# Revit family: agtatec_Record_SldngDrset_E-STA_WallBased
name_source: partatom
category: Doors
revit_build: Autodesk Revit Architecture 2015 (Build: 20140606_1530(x64)
units: mm (PartAtom-declared; Revit-internal decimal feet)

## types (12) — shared parameters
AccessoryOptions = Contact manufacturer
AcousticRating = None
AlternativeDoorsetGlazing = Part of glazing spec
AntiFingerTrapRequirement = Yes
Assembly Code = B2030110
BIMObjectName = agtatec_Record_SlidingDoorset_E-STA_WallBased
ClearHeightOfPassage = 2187.00 mm
ClearanceZones = No
Colour = Customer specific
Configuration = 1 or 2
Construction Type = Automatic Sliding Door
Description = Automatic Sliding Door
DoorIncluded = Yes
DoorOpening = 0.00 mm
DoorOpeningLeft = 1300.00 mm
DoorOpeningRight = 1300.00 mm
DoorSeal = yes
DoorsetFasteners = Screws
DoorsetOperation = Automatic
DriveDepth = 210.00 mm
DriveUnit = agtatec_Record_Sliding Door, Sheet Metal (Painted Steel)
DriveUnitExtraWidthLeft = 0.00 mm
DriveUnitExtraWidthRight = 0.00 mm
DurationUnit = year
ElectronicLock = Yes
ExtraLeft = 0.00 mm
ExtraRight = 0.00 mm
ExtraWidthLeft = 0.00 mm
ExtraWidthRight = 0.00 mm
Finish = Powder coated, Anodized, customer specific
FireExit = No
FireRating = None
FloorGuide = agtatec_Record_Sliding Door, Stainless Steel
FrameMaterial = Aluminium
FrameProfile = Aluminium
FrameSeal = Yes
GlassLayers = 2
GlassThickness1 = 6 mm (default)
GlassThickness2 = 6 mm (default)
GlassType = Part of glazing spec
GlazingAreaFraction = Depends on size. Can be calculated
HandicapAccessible = Yes
HasDrive = Yes
IfcExportAs = IfcDoorStyle
IfcExportType = Door
InnerPanelWidth = 1232.00 mm
IsExternal = Yes
LeafColourOptions = All RAL, customer specific
LeftProfile = No
ManufacturerName = Record
ManufacturerURL = www.agta-record.com
Material = Aluminium
Model = record Standard Linear Slider
ModelReference = Depends on the configuration
NBSDescription = Sliding Doorset
NBSReference = 25-50-20/175
Name = SldngDrset_THERMCORD-D-STA_WallBased_Record
NominalLength = 0.00 mm
Offset = 0.00 mm
OffsetFromInteriorWallFace(OnlyApplicableForTypesWithTwoSidePanels) = 0.00 mm
OffsetFromWallSide = 0.00 mm
OffsetFromWallTop = 0.00 mm
OpeningAxis = 1884.00 mm
OpeningWidth = 1200.00 mm
PanelFill = agtatec_Record_Sliding Door, Laminated Safety Glass (Clear)
PanelFrames = agtatec_Record_Sliding Door, Aluminium
PanelHeight = 2200.00 mm
PassageMountingProfile(OnlyApplicableForTypesWithTwoSidePanels) = No
ProductInformation = www.agta-record.com
ReferenceStandard = EN16005, EN16361, DIN 18650, etc.
ReplacementCost = Depends on the configuration and door type
RightProfile = No
SecurityRating = None
SelfClosing = Yes
ServiceLifeDuration = 10-15 years
Shape = Rectangular
SidePanelMinimumStandard = 1282.00 mm
SidePanelWidthLeft = 1300.00 mm
SidePanelWidthRight = 1300.00 mm
SmokeStop = No
SupportLength = 2493.00 mm
Thickness = 0.00 mm
ThresholdRequired = Yes
ThresholdStripping = No additional required, part of the doorset
URL = www.agta-record.com
Uniclass2 = Ss_25_30_20_77
Version = Version 1.0
WallMountingProfile = Yes
WarrantyDescription = Depends on country
WarrantyDurationLabour = Depends on country
WarrantyDurationParts = Depends on country
WarrantyDurationUnit = Depends on country
WarrantyGuarantorLabour = Local door manufacturer
WarrantyGuarantorParts = Local door manufacturer
Weight = Depends on configuration and size
WithDriveCladding = Yes
WithinStandardSizes = Yes
WithoutDriveCladding(OnlyApplicableForTypesWithoutSidePanels) = No
zero-valued in all types: Cost, ThermalTransmittance

## per-type parameters (varying)
| type | CenterOfDoor | DriveUnitHeight | Height | InterlancingProfileLeft | InterlancingProfileRight | LeftPanel | NominalHeight | NominalWidth | RightPanel | Rough Height | Rough Width | SideVoidLeft | SideVoidRight | SupportLengthLeft | SupportLengthRight | TotalHeight | TotalWidth | Width | Without side panels |
| E-STA-L 150 mm drive unit height - left - with side panel | 2514.50 mm | 150.00 mm | 2337.00 mm | Yes | No | Yes | 2337.00 mm | 2555.00 mm | No | 2343.00 mm | 2561.00 mm | 1837.00 mm | 616.00 mm | 1877.00 mm | 616.00 mm | 2337.00 mm | 2555.00 mm | 2555.00 mm | No |
| E-STA-L 150 mm drive unit height - left - without side panel | 2514.50 mm | 150.00 mm | 2337.00 mm | Yes | No | No | 2337.00 mm | 1310.00 mm | No | 2343.00 mm | 1316.00 mm | 584.00 mm | 616.00 mm | 1877.00 mm | 616.00 mm | 2337.00 mm | 1310.00 mm | 1310.00 mm | Yes |
| E-STA-R 150 mm drive unit height - right - with side panel | 1253.50 mm | 150.00 mm | 2337.00 mm | No | Yes | No | 2337.00 mm | 2555.00 mm | Yes | 2343.00 mm | 2561.00 mm | 616.00 mm | 1837.00 mm | 616.00 mm | 1877.00 mm | 2337.00 mm | 2555.00 mm | 2555.00 mm | No |
| E-STA-R 150 mm drive unit height - right - without side panel | 1253.50 mm | 150.00 mm | 2337.00 mm | No | Yes | No | 2337.00 mm | 1310.00 mm | No | 2343.00 mm | 1316.00 mm | 616.00 mm | 584.00 mm | 616.00 mm | 1877.00 mm | 2337.00 mm | 1310.00 mm | 1310.00 mm | Yes |
| E-STA-L 200 mm drive unit height - left - with side panel | 2514.50 mm | 200.00 mm | 2387.00 mm | Yes | No | Yes | 2387.00 mm | 2555.00 mm | No | 2393.00 mm | 2561.00 mm | 1837.00 mm | 616.00 mm | 1877.00 mm | 616.00 mm | 2387.00 mm | 2555.00 mm | 2555.00 mm | No |
| E-STA-L 200 mm drive unit height - left - without side panel | 2514.50 mm | 200.00 mm | 2387.00 mm | Yes | No | No | 2387.00 mm | 1310.00 mm | No | 2393.00 mm | 1316.00 mm | 584.00 mm | 616.00 mm | 1877.00 mm | 616.00 mm | 2387.00 mm | 1310.00 mm | 1310.00 mm | Yes |
| E-STA-R 200 mm drive unit height - right - with side panel | 1253.50 mm | 200.00 mm | 2387.00 mm | No | Yes | No | 2387.00 mm | 2555.00 mm | Yes | 2393.00 mm | 2561.00 mm | 616.00 mm | 1837.00 mm | 616.00 mm | 1877.00 mm | 2387.00 mm | 2555.00 mm | 2555.00 mm | No |
| E-STA-R 200 mm drive unit height - right - without side panel | 1253.50 mm | 200.00 mm | 2387.00 mm | No | Yes | No | 2387.00 mm | 1310.00 mm | No | 2393.00 mm | 1316.00 mm | 616.00 mm | 584.00 mm | 616.00 mm | 1877.00 mm | 2387.00 mm | 1310.00 mm | 1310.00 mm | Yes |
| E-STA-L 108 mm drive unit height - left - with side panel | 2514.50 mm | 108.00 mm | 2295.00 mm | Yes | No | Yes | 2295.00 mm | 2555.00 mm | No | 2301.00 mm | 2561.00 mm | 1837.00 mm | 616.00 mm | 1877.00 mm | 616.00 mm | 2295.00 mm | 2555.00 mm | 2555.00 mm | No |
| E-STA-L 108 mm drive unit height - left - without side panel | 2514.50 mm | 108.00 mm | 2295.00 mm | Yes | No | No | 2295.00 mm | 1310.00 mm | No | 2301.00 mm | 1316.00 mm | 584.00 mm | 616.00 mm | 1877.00 mm | 616.00 mm | 2295.00 mm | 1310.00 mm | 1310.00 mm | Yes |
| E-STA-R 108 mm drive unit height - right - with side panel | 1253.50 mm | 108.00 mm | 2295.00 mm | No | Yes | No | 2295.00 mm | 2555.00 mm | Yes | 2301.00 mm | 2561.00 mm | 616.00 mm | 1837.00 mm | 616.00 mm | 1877.00 mm | 2295.00 mm | 2555.00 mm | 2555.00 mm | No |
| E-STA-R 108 mm drive unit height - right - without side panel | 1253.50 mm | 108.00 mm | 2295.00 mm | No | Yes | No | 2295.00 mm | 1310.00 mm | No | 2301.00 mm | 1316.00 mm | 616.00 mm | 584.00 mm | 616.00 mm | 1877.00 mm | 2295.00 mm | 1310.00 mm | 1310.00 mm | Yes |

## geometry (parser evidence)
native form markers: Sweep x13
no freeform markers — native parametric forms only
